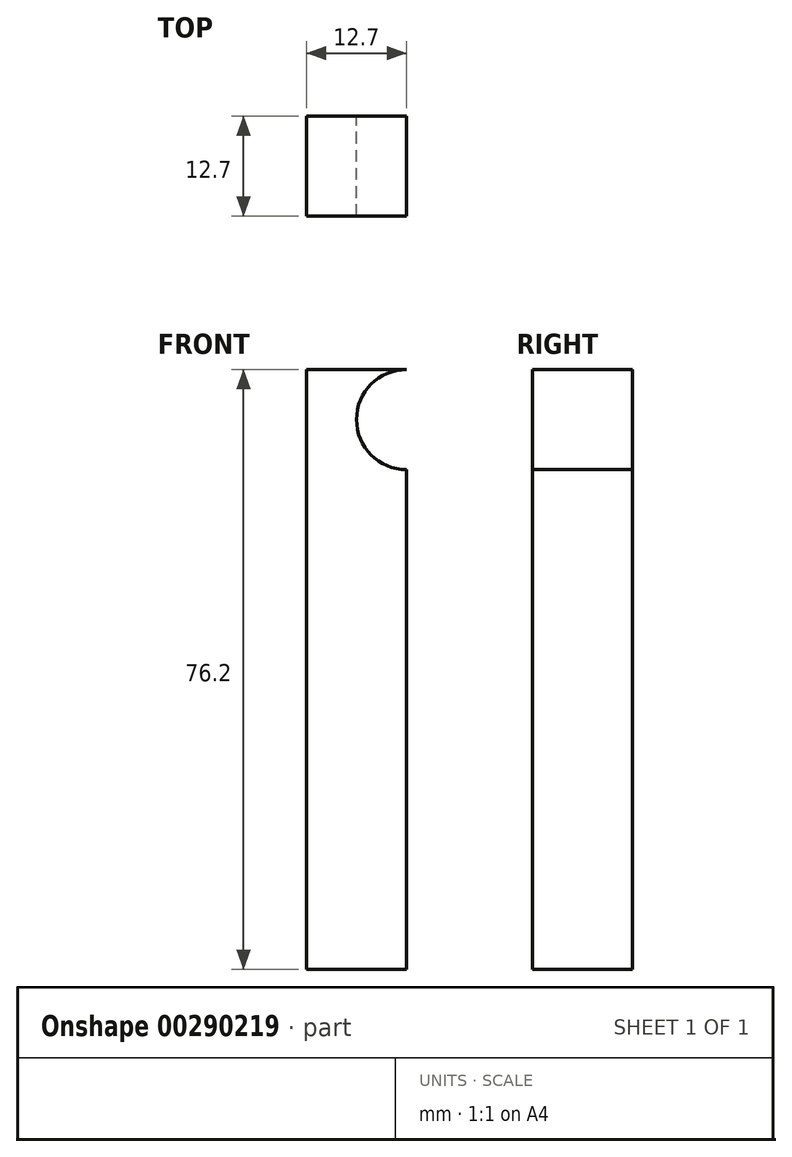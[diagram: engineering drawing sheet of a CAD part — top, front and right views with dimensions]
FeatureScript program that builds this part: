
annotation { "Feature Type Name" : "Feature", "Feature Type Description" : "" }
export const myFeature = defineFeature(function(context is Context, id is Id, definition is map)
    precondition{}
    {
        {
            var Q0;
            Q0=qCreatedBy(makeId("Front.planeOp"),FACE);
            var sketch = newSketch(context, id + "F0", { "sketchPlane" : qUnion([Q0])});
            skLineSegment(sketch, "E0", {"start": v(0, 0) * mm, "end": v(-12.7, 0) * mm});
            skLineSegment(sketch, "E1", {"start": v(-12.7, 0) * mm, "end": v(-12.7, 76.2) * mm});
            skLineSegment(sketch, "E2", {"start": v(-12.7, 76.2) * mm, "end": v(0, 76.2) * mm});
            skArc(sketch, "E3", {"start": v(0, 76.2) * mm, "mid": v(-6.35, 69.85) * mm, "end": v(0, 63.5) * mm});
            skLineSegment(sketch, "E4", {"start": v(0, 0) * mm, "end": v(0, 63.5) * mm});
            skSolve(sketch);
        }
        {
            var Q0;
            Q0=makeQuery(id+"F0.imprint","IMPRINT",FACE,{"disambiguationData":[TD([[makeQuery(id+"F0.imprint","IMPRINT",EDGE,{"derivedFrom":sQuery(id+"F0.wireOp",EDGE,"E0")}),-1.0]])]});
            extrude(context, id + "F1", {"entities" : qUnion([Q0]), "depth" : 12.7 * mm});
        }
    });
